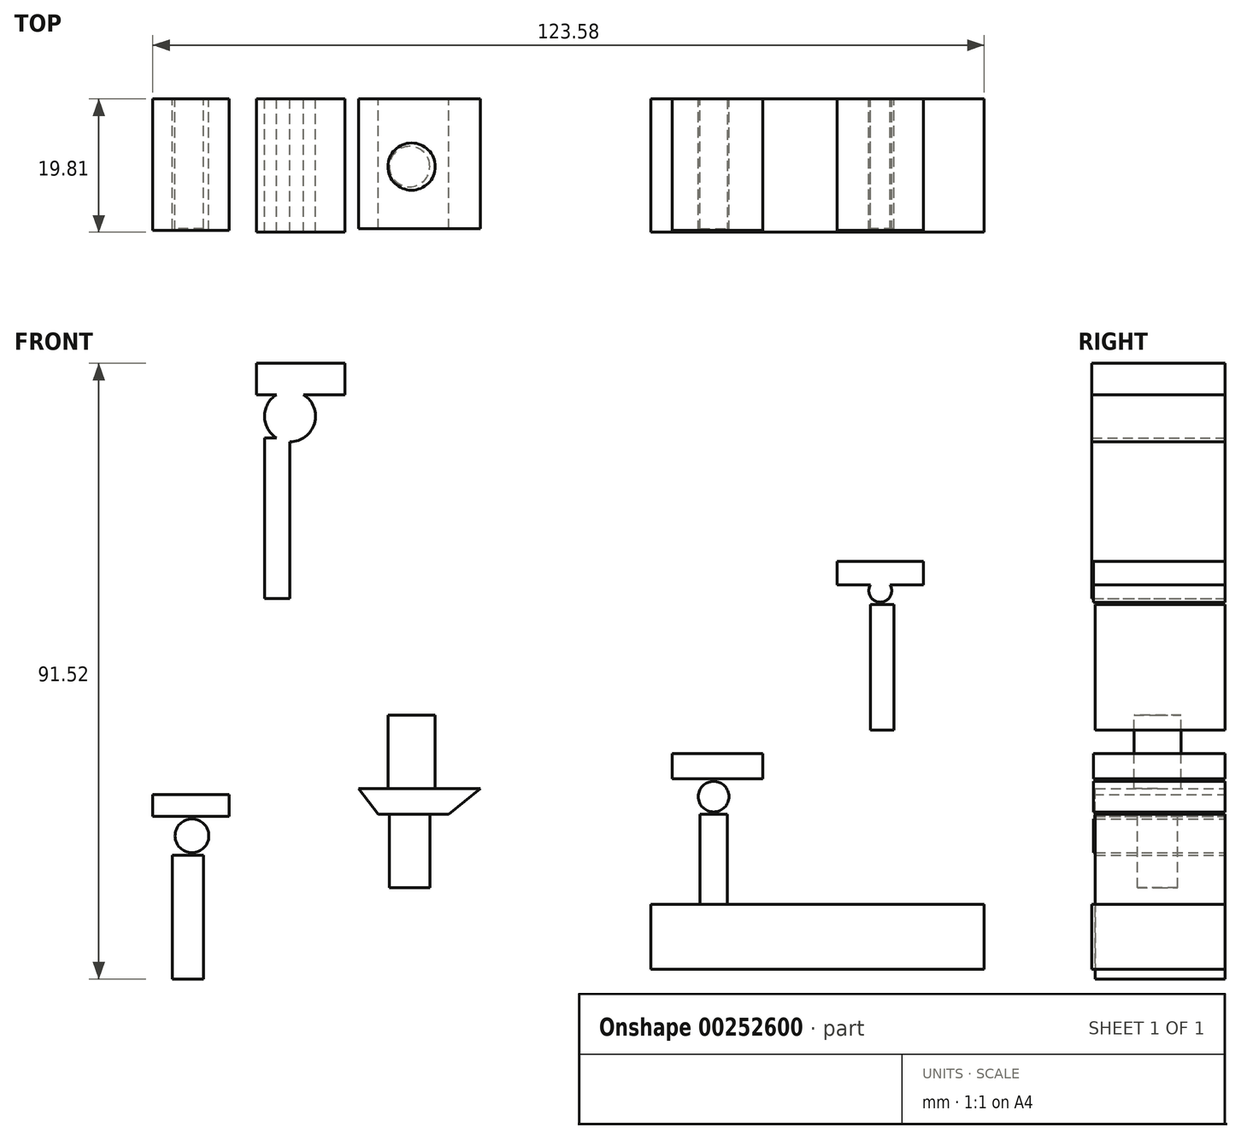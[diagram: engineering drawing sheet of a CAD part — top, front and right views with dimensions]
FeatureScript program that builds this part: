
annotation { "Feature Type Name" : "Feature", "Feature Type Description" : "" }
export const myFeature = defineFeature(function(context is Context, id is Id, definition is map)
    precondition{}
    {
        {
            var Q0;
            Q0=qCreatedBy(makeId("Front.planeOp"),FACE);
            var sketch = newSketch(context, id + "F0", { "sketchPlane" : qUnion([Q0])});
            skLineSegment(sketch, "E0", {"start": v(-69.08, -39.2) * mm, "end": v(-69.08, -20.84) * mm});
            skLineSegment(sketch, "E1", {"start": v(-69.08, -20.84) * mm, "end": v(-64.42, -20.84) * mm});
            skLineSegment(sketch, "E2", {"start": v(-64.42, -20.84) * mm, "end": v(-64.42, -33.96) * mm});
            skLineSegment(sketch, "E3", {"start": v(-64.42, -33.96) * mm, "end": v(-64.42, -39.2) * mm});
            skLineSegment(sketch, "E4", {"start": v(-64.42, -39.2) * mm, "end": v(-69.08, -39.2) * mm});
            skLineSegment(sketch, "E5", {"start": v(-38.47, -14.72) * mm, "end": v(-27.98, -14.72) * mm});
            skLineSegment(sketch, "E6", {"start": v(-27.98, -14.72) * mm, "end": v(-23.32, -10.93) * mm});
            skLineSegment(sketch, "E7", {"start": v(-23.32, -10.93) * mm, "end": v(-41.39, -10.93) * mm});
            skLineSegment(sketch, "E8", {"start": v(-38.47, -14.72) * mm, "end": v(-41.39, -10.93) * mm});
            skLineSegment(sketch, "E9", {"start": v(9.33, -29.3) * mm, "end": v(9.33, -14.72) * mm});
            skLineSegment(sketch, "E10", {"start": v(9.33, -14.72) * mm, "end": v(13.4, -14.72) * mm});
            skLineSegment(sketch, "E11", {"start": v(13.4, -14.72) * mm, "end": v(13.4, -29.3) * mm});
            skLineSegment(sketch, "E12", {"start": v(13.4, -29.3) * mm, "end": v(9.33, -29.3) * mm});
            skLineSegment(sketch, "E13", {"start": v(53.34, -24.34) * mm, "end": v(32.65, -24.34) * mm});
            skLineSegment(sketch, "E14", {"start": v(32.65, -24.34) * mm, "end": v(32.65, -33.96) * mm});
            skLineSegment(sketch, "E15", {"start": v(32.65, -33.96) * mm, "end": v(53.34, -33.96) * mm});
            skLineSegment(sketch, "E16", {"start": v(53.63, -33.08) * mm, "end": v(53.34, -24.34) * mm});
            skLineSegment(sketch, "E17", {"start": v(34.69, -2.19) * mm, "end": v(34.69, 16.47) * mm});
            skLineSegment(sketch, "E18", {"start": v(34.69, 16.47) * mm, "end": v(38.18, 16.47) * mm});
            skLineSegment(sketch, "E19", {"start": v(38.18, 16.47) * mm, "end": v(38.18, -2.19) * mm});
            skLineSegment(sketch, "E20", {"start": v(38.18, -2.19) * mm, "end": v(34.69, -2.19) * mm});
            skSolve(sketch);
        }
        {
            var Q0;
            Q0 = qSketchRegion(id + "F0", true);
            extrude(context, id + "F1", {"entities" : qUnion([Q0]), "depth" : 19.3 * mm});
        }
        {
            var Q0;
            Q0=qCreatedBy(makeId("Top.planeOp"),FACE);
            var sketch = newSketch(context, id + "F2", { "sketchPlane" : qUnion([Q0])});
            skCircle(sketch, "E21", {"center": v(-33.52, -10.06) * mm, "radius": 3.5 * mm});
            skSolve(sketch);
        }
        {
            var Q0;
            Q0 = qSketchRegion(id + "F2", true);
            extrude(context, id + "F3", {"entities" : qUnion([Q0]), "operationType" : NewBodyOperationType.ADD, "oppositeDirection" : true, "depth" : 13.72 * mm});
        }
        {
            var Q0;
            Q0=qCreatedBy(makeId("Top.planeOp"),FACE);
            var sketch = newSketch(context, id + "F4", { "sketchPlane" : qUnion([Q0])});
            skCircle(sketch, "E22", {"center": v(-33.81, -10.06) * mm, "radius": 3 * mm});
            skSolve(sketch);
        }
        {
            var Q0;
            Q0 = qSketchRegion(id + "F4", true);
            extrude(context, id + "F5", {"entities" : qUnion([Q0]), "operationType" : NewBodyOperationType.ADD, "oppositeDirection" : true, "depth" : 25.65 * mm});
        }
        {
            var Q0;
            Q0=qCreatedBy(makeId("Front.planeOp"),FACE);
            var sketch = newSketch(context, id + "F6", { "sketchPlane" : qUnion([Q0])});
            skCircle(sketch, "E23", {"center": v(11.37, -12.1) * mm, "radius": 2.28 * mm});
            skCircle(sketch, "E24", {"center": v(-66.16, -17.93) * mm, "radius": 2.5 * mm});
            skCircle(sketch, "E25", {"center": v(36.14, 18.5) * mm, "radius": 1.7 * mm});
            skSolve(sketch);
        }
        {
            var Q0;
            Q0 = qSketchRegion(id + "F6", true);
            extrude(context, id + "F7", {"entities" : qUnion([Q0]), "depth" : 19.56 * mm});
        }
        {
            var Q0;
            Q0=qCreatedBy(makeId("Front.planeOp"),FACE);
            var sketch = newSketch(context, id + "F8", { "sketchPlane" : qUnion([Q0])});
            skLineSegment(sketch, "E26.bottom", {"start": v(29.73, 22.88) * mm, "end": v(42.56, 22.88) * mm});
            skLineSegment(sketch, "E26.top", {"start": v(29.73, 19.38) * mm, "end": v(42.56, 19.38) * mm});
            skLineSegment(sketch, "E26.left", {"start": v(29.73, 22.88) * mm, "end": v(29.73, 19.38) * mm});
            skLineSegment(sketch, "E26.right", {"start": v(42.56, 22.88) * mm, "end": v(42.56, 19.38) * mm});
            skLineSegment(sketch, "E27.bottom", {"start": v(5.25, -5.68) * mm, "end": v(18.65, -5.68) * mm});
            skLineSegment(sketch, "E27.top", {"start": v(5.25, -9.47) * mm, "end": v(18.65, -9.47) * mm});
            skLineSegment(sketch, "E27.left", {"start": v(5.25, -5.68) * mm, "end": v(5.25, -9.47) * mm});
            skLineSegment(sketch, "E27.right", {"start": v(18.65, -5.68) * mm, "end": v(18.65, -9.47) * mm});
            skLineSegment(sketch, "E28.bottom", {"start": v(-72, -11.8) * mm, "end": v(-60.63, -11.8) * mm});
            skLineSegment(sketch, "E28.top", {"start": v(-72, -15.01) * mm, "end": v(-60.63, -15.01) * mm});
            skLineSegment(sketch, "E28.left", {"start": v(-72, -11.8) * mm, "end": v(-72, -15.01) * mm});
            skLineSegment(sketch, "E28.right", {"start": v(-60.63, -11.8) * mm, "end": v(-60.63, -15.01) * mm});
            skSolve(sketch);
        }
        {
            var Q0;
            Q0 = qSketchRegion(id + "F8", true);
            extrude(context, id + "F9", {"entities" : qUnion([Q0]), "operationType" : NewBodyOperationType.ADD, "depth" : 19.56 * mm});
        }
        {
            var Q0;
            Q0=qCreatedBy(makeId("Front.planeOp"),FACE);
            var sketch = newSketch(context, id + "F10", { "sketchPlane" : qUnion([Q0])});
            skLineSegment(sketch, "E29", {"start": v(-55.38, 17.34) * mm, "end": v(-55.38, 41.24) * mm});
            skLineSegment(sketch, "E30", {"start": v(-55.38, 41.24) * mm, "end": v(-51.6, 41.24) * mm});
            skLineSegment(sketch, "E31", {"start": v(-51.6, 41.24) * mm, "end": v(-51.6, 17.34) * mm});
            skLineSegment(sketch, "E32", {"start": v(-55.38, 17.34) * mm, "end": v(-51.6, 17.34) * mm});
            skCircle(sketch, "E33", {"center": v(-51.6, 44.45) * mm, "radius": 3.79 * mm});
            skLineSegment(sketch, "E34.bottom", {"start": v(-56.55, 52.32) * mm, "end": v(-43.43, 52.32) * mm});
            skLineSegment(sketch, "E34.top", {"start": v(-56.55, 47.66) * mm, "end": v(-43.43, 47.66) * mm});
            skLineSegment(sketch, "E34.left", {"start": v(-56.55, 52.32) * mm, "end": v(-56.55, 47.66) * mm});
            skLineSegment(sketch, "E34.right", {"start": v(-43.43, 52.32) * mm, "end": v(-43.43, 47.66) * mm});
            skSolve(sketch);
        }
        {
            var Q0;
            Q0 = qSketchRegion(id + "F10", true);
            extrude(context, id + "F11", {"entities" : qUnion([Q0]), "depth" : 19.8 * mm});
        }
        {
            var Q0;
            Q0=qCreatedBy(makeId("Front.planeOp"),FACE);
            var sketch = newSketch(context, id + "F12", { "sketchPlane" : qUnion([Q0])});
            skLineSegment(sketch, "E35.bottom", {"start": v(2.04, -28.13) * mm, "end": v(51.6, -28.13) * mm});
            skLineSegment(sketch, "E35.top", {"start": v(2.04, -37.75) * mm, "end": v(51.6, -37.75) * mm});
            skLineSegment(sketch, "E35.left", {"start": v(2.04, -28.13) * mm, "end": v(2.04, -37.75) * mm});
            skLineSegment(sketch, "E35.right", {"start": v(51.6, -28.13) * mm, "end": v(51.6, -37.75) * mm});
            skSolve(sketch);
        }
        {
            var Q0;
            Q0 = qSketchRegion(id + "F12", true);
            extrude(context, id + "F13", {"entities" : qUnion([Q0]), "operationType" : NewBodyOperationType.ADD, "depth" : 19.8 * mm});
        }
    });
